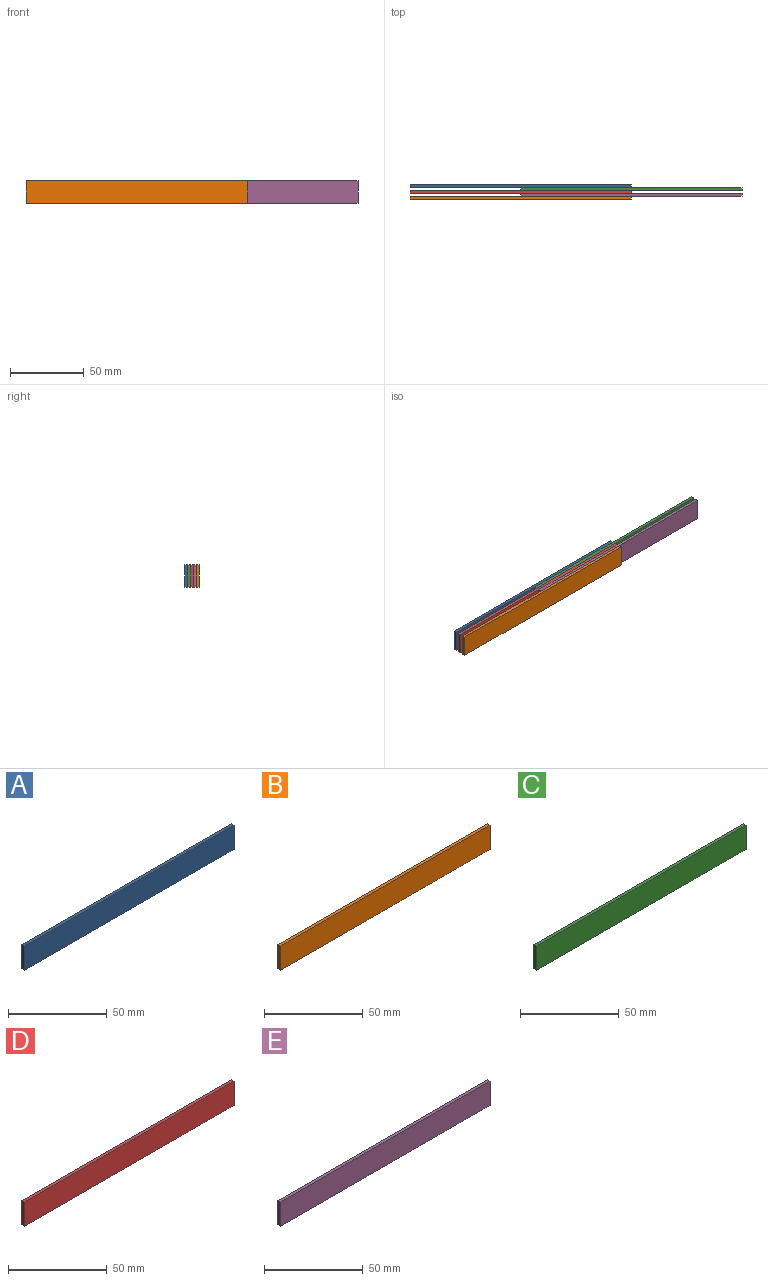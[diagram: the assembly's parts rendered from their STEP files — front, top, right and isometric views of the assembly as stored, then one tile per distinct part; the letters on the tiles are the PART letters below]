
ASSEMBLY  parts=5 mates=4
PART A: 6 faces, bbox 150x2x15 mm
  f0: plane 150x2mm, normal (0,0,-1), area 300mm2, adj f1,f3,f4,f5
  f1: plane 15x2mm, normal (1,0,0), area 30mm2, adj f0,f2,f4,f5
  f2: plane 150x2mm, normal (0,0,1), area 300mm2, adj f1,f3,f4,f5
  f3: plane 15x2mm, normal (-1,0,0), area 30mm2, adj f0,f2,f4,f5
  f4: plane 150x15mm, normal (0,-1,0), area 2250mm2, adj f0,f1,f2,f3
  f5: plane 150x15mm, normal (0,1,0), area 2250mm2, adj f0,f1,f2,f3
PART B: 6 faces, bbox 150x2x15 mm
  f0: plane 150x2mm, normal (0,0,-1), area 300mm2, adj f1,f3,f4,f5
  f1: plane 15x2mm, normal (1,0,0), area 30mm2, adj f0,f2,f4,f5
  f2: plane 150x2mm, normal (0,0,1), area 300mm2, adj f1,f3,f4,f5
  f3: plane 15x2mm, normal (-1,0,0), area 30mm2, adj f0,f2,f4,f5
  f4: plane 150x15mm, normal (0,-1,0), area 2250mm2, adj f0,f1,f2,f3
  f5: plane 150x15mm, normal (0,1,0), area 2250mm2, adj f0,f1,f2,f3
PART C: 6 faces, bbox 150x2x15 mm
  f0: plane 150x2mm, normal (0,0,-1), area 300mm2, adj f1,f3,f4,f5
  f1: plane 15x2mm, normal (1,0,0), area 30mm2, adj f0,f2,f4,f5
  f2: plane 150x2mm, normal (0,0,1), area 300mm2, adj f1,f3,f4,f5
  f3: plane 15x2mm, normal (-1,0,0), area 30mm2, adj f0,f2,f4,f5
  f4: plane 150x15mm, normal (0,-1,0), area 2250mm2, adj f0,f1,f2,f3
  f5: plane 150x15mm, normal (0,1,0), area 2250mm2, adj f0,f1,f2,f3
PART D: 6 faces, bbox 150x2x15 mm
  f0: plane 150x2mm, normal (0,0,-1), area 300mm2, adj f1,f3,f4,f5
  f1: plane 15x2mm, normal (1,0,0), area 30mm2, adj f0,f2,f4,f5
  f2: plane 150x2mm, normal (0,0,1), area 300mm2, adj f1,f3,f4,f5
  f3: plane 15x2mm, normal (-1,0,0), area 30mm2, adj f0,f2,f4,f5
  f4: plane 150x15mm, normal (0,-1,0), area 2250mm2, adj f0,f1,f2,f3
  f5: plane 150x15mm, normal (0,1,0), area 2250mm2, adj f0,f1,f2,f3
PART E: 6 faces, bbox 150x2x15 mm
  f0: plane 150x2mm, normal (0,0,-1), area 300mm2, adj f1,f3,f4,f5
  f1: plane 15x2mm, normal (1,0,0), area 30mm2, adj f0,f2,f4,f5
  f2: plane 150x2mm, normal (0,0,1), area 300mm2, adj f1,f3,f4,f5
  f3: plane 15x2mm, normal (-1,0,0), area 30mm2, adj f0,f2,f4,f5
  f4: plane 150x15mm, normal (0,-1,0), area 2250mm2, adj f0,f1,f2,f3
  f5: plane 150x15mm, normal (0,1,0), area 2250mm2, adj f0,f1,f2,f3
PLACE A t=(-12.58,-3.43,4.24)mm fixed
PLACE B t=(-12.58,4.57,4.24)mm
PLACE C t=(62.42,-1.43,4.24)mm
PLACE D t=(-12.58,0.57,4.24)mm
PLACE E t=(62.42,2.57,4.24)mm
MATE planar D.f5 <-> C.f4  axis (0,1,0) through (62.42,-7.43,4.24)mm
MATE planar D.f4 <-> E.f5  axis (0,-1,0) through (62.42,-9.43,4.24)mm
MATE planar E.f4 <-> B.f5  axis (0,-1,0) through (62.42,-11.43,4.24)mm
MATE planar A.f4 <-> C.f5  axis (0,-1,0) through (-12.58,-5.43,4.24)mm
